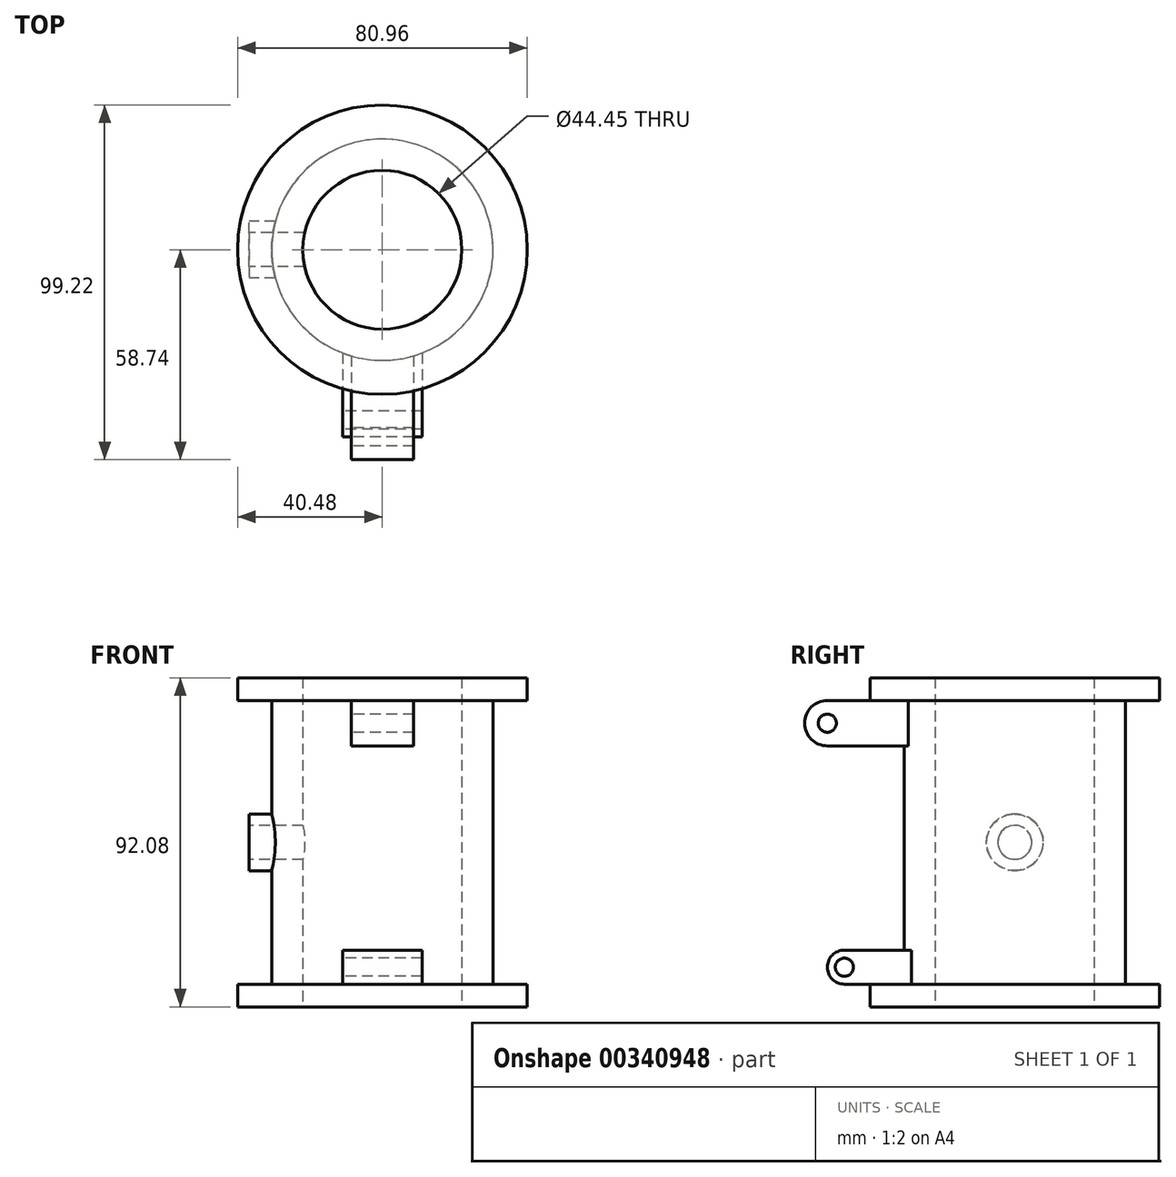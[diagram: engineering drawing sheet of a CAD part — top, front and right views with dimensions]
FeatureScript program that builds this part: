
annotation { "Feature Type Name" : "Feature", "Feature Type Description" : "" }
export const myFeature = defineFeature(function(context is Context, id is Id, definition is map)
    precondition{}
    {
        {
            var Q0;
            Q0=qCreatedBy(makeId("Top.planeOp"),FACE);
            var sketch = newSketch(context, id + "F0", { "sketchPlane" : qUnion([Q0])});
            skCircle(sketch, "E0", {"center": v(0, 0) * mm, "radius": 22.23 * mm});
            skCircle(sketch, "E1", {"center": v(0, 0) * mm, "radius": 30.96 * mm});
            skSolve(sketch);
        }
        {
            var Q0;
            Q0 = qSketchRegion(id + "F0", true);
            extrude(context, id + "F1", {"entities" : qUnion([Q0]), "depth" : 92.07 * mm});
        }
        {
            var Q0;
            Q0=makeQuery(id+"F1.opExtrude","CAP_FACE",FACE,{"disambiguationData":[OSD([sQuery(id+"F0.wireOp",EDGE,"E0"),sQuery(id+"F0.wireOp",EDGE,"E1")])],"isStart":false});
            var sketch = newSketch(context, id + "F2", { "sketchPlane" : qUnion([Q0])});
            skCircle(sketch, "E2.0", {"center": v(0, 0) * mm, "radius": 30.96 * mm});
            skCircle(sketch, "E3.0", {"center": v(0, 0) * mm, "radius": 40.48 * mm});
            skSolve(sketch);
        }
        {
            var Q0;
            Q0 = qSketchRegion(id + "F2", true);
            extrude(context, id + "F3", {"entities" : qUnion([Q0]), "operationType" : NewBodyOperationType.ADD, "oppositeDirection" : true, "depth" : 6.35 * mm});
        }
        {
            var Q0;
            Q0=makeQuery(id+"F1.opExtrude","CAP_FACE",FACE,{"disambiguationData":[OSD([sQuery(id+"F0.wireOp",EDGE,"E0"),sQuery(id+"F0.wireOp",EDGE,"E1")])],"isStart":true});
            var sketch = newSketch(context, id + "F4", { "sketchPlane" : qUnion([Q0])});
            skCircle(sketch, "E4.0", {"center": v(0, 0) * mm, "radius": 30.96 * mm});
            skCircle(sketch, "E5.0", {"center": v(0, 0) * mm, "radius": 40.48 * mm});
            skSolve(sketch);
        }
        {
            var Q0;
            Q0 = qSketchRegion(id + "F4", true);
            extrude(context, id + "F5", {"entities" : qUnion([Q0]), "operationType" : NewBodyOperationType.ADD, "oppositeDirection" : true, "depth" : 6.35 * mm});
        }
        {
            var Q0;
            Q0=qCreatedBy(makeId("Front.planeOp"),FACE);
            cPlane(context, id + "F6", {"entities" : qUnion([Q0]), "cplaneType" : CPlaneType.OFFSET, "offset" : 58.74 * mm, "width" : 152.4 * mm, "height" : 152.4 * mm});
        }
        {
            var Q0;
            Q0=qCreatedBy(id+"F6.planeOp",FACE);
            var sketch = newSketch(context, id + "F7", { "sketchPlane" : qUnion([Q0])});
            skLineSegment(sketch, "E6", {"start": v(0, 73.03) * mm, "end": v(8.73, 73.03) * mm});
            skLineSegment(sketch, "E7", {"start": v(8.73, 73.03) * mm, "end": v(8.73, 85.73) * mm});
            skLineSegment(sketch, "E8", {"start": v(0, 73.03) * mm, "end": v(-8.73, 73.03) * mm});
            skLineSegment(sketch, "E9", {"start": v(-8.73, 73.03) * mm, "end": v(-8.73, 85.73) * mm});
            skLineSegment(sketch, "E10", {"start": v(-8.73, 85.73) * mm, "end": v(8.73, 85.73) * mm});
            skSolve(sketch);
        }
        {
            var Q0;
            Q0 = qSketchRegion(id + "F7", true);
            var Q1;
            Q1=makeQuery(id+"F1.opExtrude","SWEPT_BODY",BODY,{"disambiguationData":[OSD([sQuery(id+"F0.wireOp",EDGE,"E0"),sQuery(id+"F0.wireOp",EDGE,"E1")])]});
            extrude(context, id + "F8", {"entities" : qUnion([Q0]), "operationType" : NewBodyOperationType.ADD, "endBound" : BoundingType.UP_TO_BODY, "oppositeDirection" : true, "endBoundEntityBody" : qUnion([Q1]), "depth" : 25.4 * mm});
        }
        {
            var Q0;
            Q0=qCreatedBy(makeId("Front.planeOp"),FACE);
            cPlane(context, id + "F9", {"entities" : qUnion([Q0]), "cplaneType" : CPlaneType.OFFSET, "offset" : 52.4 * mm, "width" : 152.4 * mm, "height" : 152.4 * mm});
        }
        {
            var Q0;
            Q0=qCreatedBy(id+"F9.planeOp",FACE);
            var sketch = newSketch(context, id + "F10", { "sketchPlane" : qUnion([Q0])});
            skLineSegment(sketch, "E11", {"start": v(0, 15.88) * mm, "end": v(11.11, 15.88) * mm});
            skLineSegment(sketch, "E12", {"start": v(11.11, 15.88) * mm, "end": v(11.11, 6.35) * mm});
            skLineSegment(sketch, "E13", {"start": v(0, 15.88) * mm, "end": v(-11.13, 15.88) * mm});
            skLineSegment(sketch, "E14", {"start": v(-11.13, 15.88) * mm, "end": v(-11.13, 6.35) * mm});
            skLineSegment(sketch, "E15", {"start": v(-11.13, 6.35) * mm, "end": v(11.11, 6.35) * mm});
            skSolve(sketch);
        }
        {
            var Q0;
            Q0 = qSketchRegion(id + "F10", true);
            var Q1;
            Q1=makeQuery(id+"F1.opExtrude","SWEPT_BODY",BODY,{"disambiguationData":[OSD([sQuery(id+"F0.wireOp",EDGE,"E0"),sQuery(id+"F0.wireOp",EDGE,"E1")])]});
            extrude(context, id + "F11", {"entities" : qUnion([Q0]), "operationType" : NewBodyOperationType.ADD, "endBound" : BoundingType.UP_TO_BODY, "oppositeDirection" : true, "endBoundEntityBody" : qUnion([Q1]), "depth" : 25.4 * mm});
        }
        {
            var Q0;
            Q0=qCreatedBy(makeId("Right.planeOp"),FACE);
            cPlane(context, id + "F12", {"entities" : qUnion([Q0]), "cplaneType" : CPlaneType.OFFSET, "offset" : 37.3 * mm, "oppositeDirection" : true, "width" : 152.4 * mm, "height" : 152.4 * mm});
        }
        {
            var Q0;
            Q0=qCreatedBy(id+"F12.planeOp",FACE);
            var sketch = newSketch(context, id + "F13", { "sketchPlane" : qUnion([Q0])});
            skCircle(sketch, "E16", {"center": v(0, 46.04) * mm, "radius": 7.94 * mm});
            skSolve(sketch);
        }
        {
            var Q0;
            Q0 = qSketchRegion(id + "F13", true);
            var Q1;
            Q1=makeQuery(id+"F1.opExtrude","SWEPT_BODY",BODY,{"disambiguationData":[OSD([sQuery(id+"F0.wireOp",EDGE,"E0"),sQuery(id+"F0.wireOp",EDGE,"E1")])]});
            extrude(context, id + "F14", {"entities" : qUnion([Q0]), "operationType" : NewBodyOperationType.ADD, "endBound" : BoundingType.UP_TO_BODY, "endBoundEntityBody" : qUnion([Q1]), "depth" : 25.4 * mm});
        }
        {
            var Q0;
            Q0=makeQuery(id+"F8.opExtrude","SWEPT_FACE",FACE,{"disambiguationData":[OSD([sQuery(id+"F7.wireOp",EDGE,"E9")])]});
            var sketch = newSketch(context, id + "F15", { "sketchPlane" : qUnion([Q0])});
            skArc(sketch, "E17", {"start": v(52.39, 73.03) * mm, "mid": v(58.74, 79.38) * mm, "end": v(52.39, 85.72) * mm});
            skCircle(sketch, "E18", {"center": v(52.39, 79.38) * mm, "radius": 2.54 * mm});
            skLineSegment(sketch, "E19.0", {"start": v(58.74, 73.03) * mm, "end": v(58.74, 85.73) * mm});
            skLineSegment(sketch, "E20.0", {"start": v(52.39, 85.73) * mm, "end": v(58.74, 85.73) * mm});
            skLineSegment(sketch, "E21.0", {"start": v(52.39, 73.03) * mm, "end": v(58.74, 73.03) * mm});
            skSolve(sketch);
        }
        {
            var Q0;
            Q0 = qSketchRegion(id + "F15", true);
            var Q1;
            Q1=makeQuery(id+"F8.opExtrude","SWEPT_FACE",FACE,{"disambiguationData":[OSD([sQuery(id+"F7.wireOp",EDGE,"E7")])]});
            extrude(context, id + "F16", {"entities" : qUnion([Q0]), "operationType" : NewBodyOperationType.REMOVE, "endBound" : BoundingType.UP_TO_SURFACE, "oppositeDirection" : true, "endBoundEntityFace" : qUnion([Q1]), "depth" : 25.4 * mm});
        }
        {
            var Q0;
            Q0=makeQuery(id+"F11.opExtrude","SWEPT_FACE",FACE,{"disambiguationData":[OSD([sQuery(id+"F10.wireOp",EDGE,"E14")])]});
            var sketch = newSketch(context, id + "F17", { "sketchPlane" : qUnion([Q0])});
            skArc(sketch, "E22", {"start": v(47.62, 6.35) * mm, "mid": v(52.39, 11.11) * mm, "end": v(47.62, 15.87) * mm});
            skLineSegment(sketch, "E23.0", {"start": v(47.62, 15.87) * mm, "end": v(52.39, 15.87) * mm});
            skLineSegment(sketch, "E24.0", {"start": v(47.62, 6.35) * mm, "end": v(52.39, 6.35) * mm});
            skLineSegment(sketch, "E25.0", {"start": v(52.39, 15.87) * mm, "end": v(52.39, 6.35) * mm});
            skCircle(sketch, "E26", {"center": v(47.62, 11.11) * mm, "radius": 2.54 * mm});
            skSolve(sketch);
        }
        {
            var Q0;
            Q0 = qSketchRegion(id + "F17", true);
            var Q1;
            Q1=makeQuery(id+"F11.opExtrude","SWEPT_FACE",FACE,{"disambiguationData":[OSD([sQuery(id+"F10.wireOp",EDGE,"E12")])]});
            extrude(context, id + "F18", {"entities" : qUnion([Q0]), "operationType" : NewBodyOperationType.REMOVE, "endBound" : BoundingType.UP_TO_SURFACE, "oppositeDirection" : true, "endBoundEntityFace" : qUnion([Q1]), "depth" : 25.4 * mm});
        }
        {
            var Q0;
            Q0=makeQuery(id+"F14.opExtrude","CAP_FACE",FACE,{"disambiguationData":[OSD([sQuery(id+"F13.wireOp",EDGE,"E16")])],"isStart":true});
            var sketch = newSketch(context, id + "F19", { "sketchPlane" : qUnion([Q0])});
            skCircle(sketch, "E27", {"center": v(0, 46.04) * mm, "radius": 4.76 * mm});
            skSolve(sketch);
        }
        {
            var Q0;
            Q0 = qSketchRegion(id + "F19", true);
            extrude(context, id + "F20", {"entities" : qUnion([Q0]), "operationType" : NewBodyOperationType.REMOVE, "oppositeDirection" : true, "depth" : 16 * mm});
        }
    });
